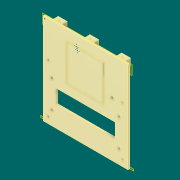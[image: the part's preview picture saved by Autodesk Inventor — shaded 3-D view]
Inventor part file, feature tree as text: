
AUTODESK INVENTOR PART (.ipt)
format: ipt  version: 2019 (Build 230136000, 136)  size: 352,768 bytes
history: native  units: mm
features: sketch x33, extrude x30, reference x17, other x6, plane x2
ambient origin geometry x8: Origin, YZ Plane, XZ Plane, XY Plane, X Axis, Y Axis, Z Axis, Center Point
bodies: Solid1 (feature_tree)
feature tree (88):
  plane  "Work Plane1"
  extrude  "Extrusion1"  Depth=8.0mm
  extrude  "Extrusion2"  Depth=8.0mm
  extrude  "Extrusion3"  Depth=5.0mm
  plane  "Work Plane2"
  extrude  "Extrusion4"  Depth=8.0mm TaperAngle=0.0deg
  extrude  "Extrusion5"  Depth=1.5mm
  extrude  "Extrusion6"  Depth=8.0mm TaperAngle=0.0deg
  extrude  "Extrusion7"  Depth=10.0mm
  extrude  "Extrusion8"  Depth=10.0mm
  extrude  "Extrusion9"  Depth=10.0mm
  extrude  "Extrusion10"  Depth=10.0mm
  extrude  "Extrusion11"  Depth=1.5mm
  extrude  "Extrusion12"  Depth=1.5mm
  extrude  "Extrusion13"  Depth=2.0mm TaperAngle=0.0deg
  extrude  "Extrusion14"  Depth=16.0mm
  sketch  "Sketch15"  dims[d43=66.0mm d44=2.0mm d45=0.0mm]
  extrude  "Extrusion15"  Depth=2.0mm TaperAngle=0.0deg
  extrude  "Extrusion16"  Depth=2.75mm
  extrude  "Extrusion17"  Depth=2.75mm
  extrude  "Extrusion18"  Depth=2.0mm TaperAngle=0.0deg
  extrude  "Extrusion19"  Depth=16.0mm
  extrude  "Extrusion20"  Depth=16.0mm
  extrude  "Extrusion21"  Depth=2.75mm
  sketch  "Sketch23"  dims[d89=2.75mm d92=2.75mm]
  extrude  "Extrusion22"  Depth=5.4mm
  extrude  "Extrusion23"  Depth=2.75mm
  extrude  "Extrusion24"  Depth=2.0mm TaperAngle=0.0deg
  sketch  "Sketch27"  dims[d118=3.0mm d119=2.0mm d120=0.0mm]
  extrude  "Extrusion25"  Depth=5.5mm
  extrude  "Extrusion26"  Depth=2.0mm TaperAngle=0.0deg
  extrude  "Extrusion27"  Depth=2.0mm TaperAngle=0.0deg
  extrude  "Extrusion28"  Depth=3.0mm
  extrude  "Extrusion29"  Depth=3.0mm
  extrude  "Extrusion30"  Depth=2.0mm TaperAngle=0.0deg
  sketch  "Sketch1"  dims[d0=10.0mm d1=8.0mm]
  reference  "Reference1"
  reference  "Reference2"
  reference  "Reference3"
  reference  "Reference4"
  reference  "Reference5"
  sketch  "Sketch2"  dims[d3=10.0mm d4=8.0mm]
  sketch  "Sketch3"  dims[d5=8.0mm d6=0.0mm d7=5.0mm]
  sketch  "Sketch4"  dims[d8=10.0mm d9=8.0mm d10=0.0mm]
  reference  "Reference6"
  reference  "Reference7"
  reference  "Reference8"
  sketch  "Sketch5"  dims[d12=1.5mm d14=1.5mm]
  sketch  "Sketch6"  dims[d16=1.5mm d17=8.0mm d18=0.0mm]
  reference  "Reference9"
  reference  "Reference10"
  reference  "Reference11"
  reference  "Reference12"
  reference  "Reference13"
  reference  "Reference14"
  sketch  "Sketch7"  dims[d19=10.0mm d20=10.0mm]
  sketch  "Sketch8"  dims[d21=10.0mm d22=10.0mm]
  sketch  "Sketch9"  dims[d24=5.0mm d25=10.0mm]
  sketch  "Sketch10"  dims[d26=10.0mm d27=10.0mm]
  sketch  "Sketch11"  dims[d28=8.0mm d29=0.0mm d31=1.5mm]
  sketch  "Sketch12"  dims[d33=1.5mm d35=1.5mm]
  sketch  "Sketch13"  dims[d36=10.0mm d37=0.0mm d38=2.0mm d39=0.0mm]
  sketch  "Sketch14"  dims[d41=33.0mm d42=16.0mm]
  sketch  "Sketch16"  dims[d50=2.75mm d54=2.75mm]
  sketch  "Sketch17"  dims[d61=2.75mm d64=2.75mm]
  sketch  "Sketch18"  dims[d65=2.0mm d66=0.0mm d67=2.0mm d68=0.0mm]
  sketch  "Sketch19"  dims[d70=33.0mm d71=16.0mm]
  sketch  "Sketch20"  dims[d72=66.0mm d73=16.0mm]
  sketch  "Sketch21"  dims[d74=33.0mm d80=2.75mm]
  sketch  "Sketch22"  dims[d83=2.75mm d84=5.4mm]
  sketch  "Sketch24"  dims[d93=2.0mm d94=0.0mm d96=2.0mm d97=0.0mm]
  reference  "Reference15"
  sketch  "Sketch25"  dims[d98=2.0mm d99=0.0mm d104=5.5mm]
  sketch  "Sketch26"  dims[d110=2.0mm d111=0.0mm d112=2.0mm d113=0.0mm]
  sketch  "Sketch28"  dims[d121=2.0mm d122=0.0mm d127=3.0mm]
  reference  "Reference16"
  sketch  "Sketch29"  dims[d128=2.0mm d129=0.0mm d134=3.0mm]
  reference  "Reference17"
  sketch  "Sketch30"  dims[d135=2.0mm d136=0.0mm d137=2.0mm d138=0.0mm]
  sketch  "Sketch31"  dims[d143=3.0mm]
  sketch  "Sketch32"  dims[d147=3.0mm]
  sketch  "Sketch33"  dims[d150=33.0mm d151=16.0mm d152=66.0mm d157=3.0mm d161=3.0mm d162=2.0mm d163=0.0mm d164=2.0mm d165=0.0mm d166=2.0mm d167=0.0mm d168=2.5mm d169=2.0mm d170=0.0mm d171=2.5mm d172=2.5mm d173=2.0mm d174=0.0mm d175=2.5mm d176=2.0mm d177=0.0mm d178=2.0mm d179=0.0mm d180=40.0mm d181=40.0mm d182=1.0mm d183=0.5mm d184=0.0mm d185=1.0mm d186=11.0mm d187=1.5mm d188=0.0mm d189=0.5mm d190=0.0mm d191=1.0mm d192=1.5mm d193=0.0mm]
  other  "Ensamblaje Reloj LCD 16x2.iam"
  other  "Down:1"
  other  "Lado izquierdo:1"
  other  "Lateral Derecho:1"
  other  "UP:1"
  other  "PCB Front:1"
